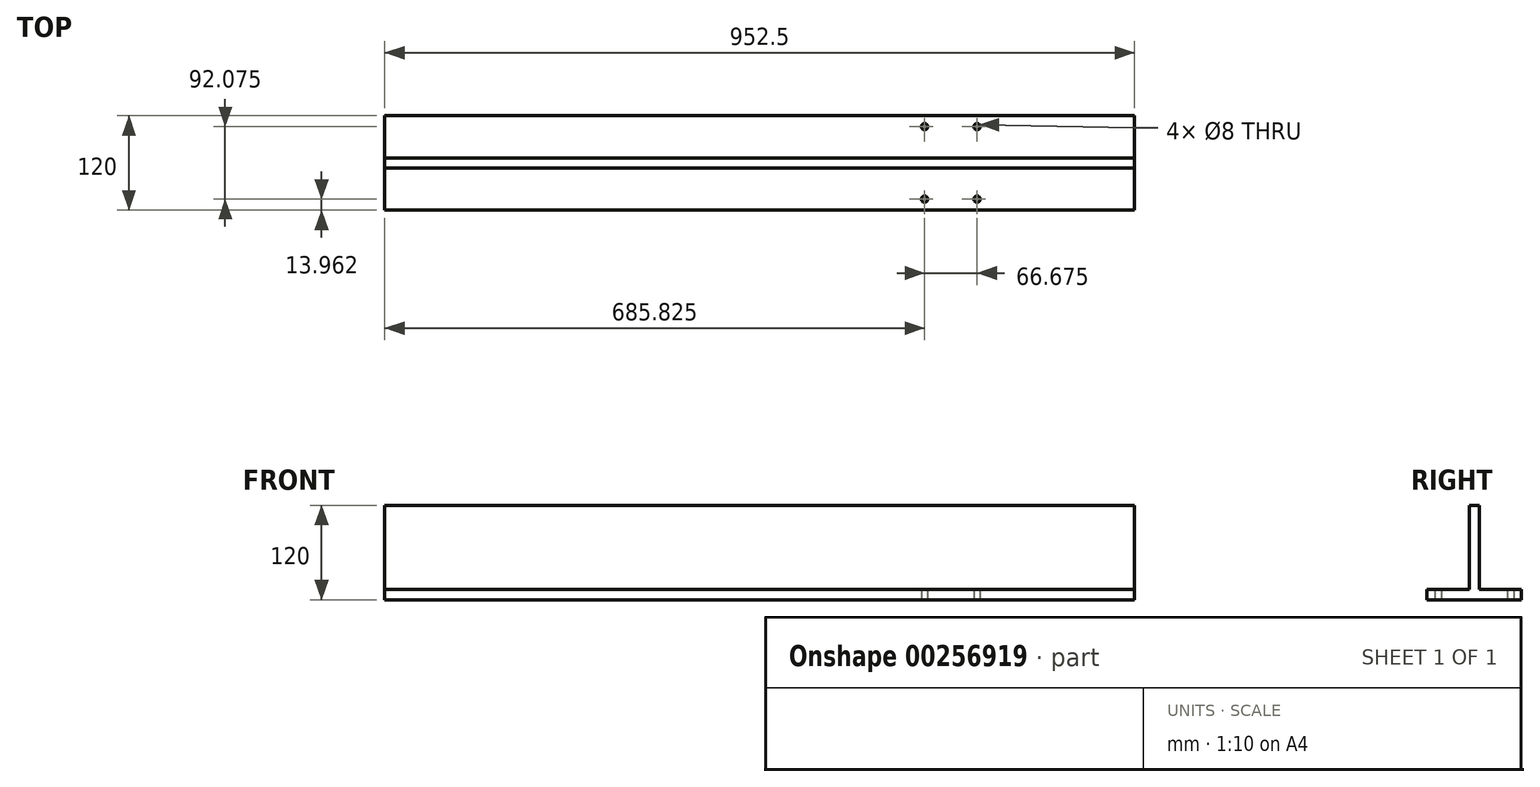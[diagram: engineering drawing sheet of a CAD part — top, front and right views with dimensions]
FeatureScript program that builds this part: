
annotation { "Feature Type Name" : "Feature", "Feature Type Description" : "" }
export const myFeature = defineFeature(function(context is Context, id is Id, definition is map)
    precondition{}
    {
        {
            var Q0;
            Q0=qCreatedBy(makeId("Right.planeOp"),FACE);
            var sketch = newSketch(context, id + "F0", { "sketchPlane" : qUnion([Q0])});
            skLineSegment(sketch, "E0", {"start": v(-60, 0) * mm, "end": v(60, 0) * mm});
            skLineSegment(sketch, "E1", {"start": v(60, 0) * mm, "end": v(60, 13) * mm});
            skLineSegment(sketch, "E2", {"start": v(60, 13) * mm, "end": v(6.5, 13) * mm});
            skLineSegment(sketch, "E3", {"start": v(6.5, 13) * mm, "end": v(6.5, 120) * mm});
            skLineSegment(sketch, "E4", {"start": v(6.5, 120) * mm, "end": v(-6.5, 120) * mm});
            skLineSegment(sketch, "E5", {"start": v(-6.5, 120) * mm, "end": v(-6.5, 13) * mm});
            skLineSegment(sketch, "E6", {"start": v(-6.5, 13) * mm, "end": v(-60, 13) * mm});
            skLineSegment(sketch, "E7", {"start": v(-60, 13) * mm, "end": v(-60, 0) * mm});
            skPoint(sketch, "E8", {"position": v(0, 120) * mm});
            skSolve(sketch);
        }
        {
            var Q0;
            Q0=makeQuery(id+"F0.imprint","IMPRINT",FACE,{"disambiguationData":[TD([[makeQuery(id+"F0.imprint","IMPRINT",EDGE,{"derivedFrom":sQuery(id+"F0.wireOp",EDGE,"E0")}),1.0]])]});
            extrude(context, id + "F1", {"entities" : qUnion([Q0]), "oppositeDirection" : true, "depth" : 952.5 * mm});
        }
        {
            var Q0;
            Q0=qCreatedBy(makeId("Top.planeOp"),FACE);
            var sketch = newSketch(context, id + "F2", { "sketchPlane" : qUnion([Q0])});
            skCircle(sketch, "E9", {"center": v(-200, 46.04) * mm, "radius": 4 * mm});
            skCircle(sketch, "E10", {"center": v(-266.68, 46.04) * mm, "radius": 4 * mm});
            skCircle(sketch, "E11", {"center": v(-266.68, -46.04) * mm, "radius": 4 * mm});
            skCircle(sketch, "E12", {"center": v(-200, -46.04) * mm, "radius": 4 * mm});
            skLineSegment(sketch, "E13", {"start": v(-476.25, 0) * mm, "end": v(-476.25, 155.08) * mm, "construction": true});
            skCircle(sketch, "E14.MirrorC", {"center": v(-685.83, -46.04) * mm, "radius": 4 * mm});
            skCircle(sketch, "E15.MirrorC", {"center": v(-752.5, -46.04) * mm, "radius": 4 * mm});
            skCircle(sketch, "E16.MirrorC", {"center": v(-752.5, 46.04) * mm, "radius": 4 * mm});
            skCircle(sketch, "E17.MirrorC", {"center": v(-685.83, 46.04) * mm, "radius": 4 * mm});
            skSolve(sketch);
        }
        {
            var Q0;
            Q0=makeQuery(id+"F2.imprint","IMPRINT",FACE,{"disambiguationData":[TD([[makeQuery(id+"F2.imprint","IMPRINT",EDGE,{"derivedFrom":sQuery(id+"F2.wireOp",EDGE,"E12")}),1.0]])]});
            var Q1;
            Q1=makeQuery(id+"F2.imprint","IMPRINT",FACE,{"disambiguationData":[TD([[makeQuery(id+"F2.imprint","IMPRINT",EDGE,{"derivedFrom":sQuery(id+"F2.wireOp",EDGE,"E9")}),1.0]])]});
            var Q2;
            Q2=makeQuery(id+"F2.imprint","IMPRINT",FACE,{"disambiguationData":[TD([[makeQuery(id+"F2.imprint","IMPRINT",EDGE,{"derivedFrom":sQuery(id+"F2.wireOp",EDGE,"E10")}),1.0]])]});
            var Q3;
            Q3=makeQuery(id+"F2.imprint","IMPRINT",FACE,{"disambiguationData":[TD([[makeQuery(id+"F2.imprint","IMPRINT",EDGE,{"derivedFrom":sQuery(id+"F2.wireOp",EDGE,"E11")}),1.0]])]});
            var Q4;
            Q4=makeQuery(id+"F2.imprint","IMPRINT",FACE,{"disambiguationData":[TD([[makeQuery(id+"F2.imprint","IMPRINT",EDGE,{"derivedFrom":sQuery(id+"F2.wireOp",EDGE,"E15.MirrorC")}),-1.0]])]});
            var Q5;
            Q5=makeQuery(id+"F2.imprint","IMPRINT",FACE,{"disambiguationData":[TD([[makeQuery(id+"F2.imprint","IMPRINT",EDGE,{"derivedFrom":sQuery(id+"F2.wireOp",EDGE,"E14.MirrorC")}),-1.0]])]});
            var Q6;
            Q6=makeQuery(id+"F2.imprint","IMPRINT",FACE,{"disambiguationData":[TD([[makeQuery(id+"F2.imprint","IMPRINT",EDGE,{"derivedFrom":sQuery(id+"F2.wireOp",EDGE,"E17.MirrorC")}),-1.0]])]});
            var Q7;
            Q7=makeQuery(id+"F2.imprint","IMPRINT",FACE,{"disambiguationData":[TD([[makeQuery(id+"F2.imprint","IMPRINT",EDGE,{"derivedFrom":sQuery(id+"F2.wireOp",EDGE,"E16.MirrorC")}),-1.0]])]});
            var Q8;
            Q8=sQuery(id+"F2.wireOp",EDGE,"E11");
            var Q9;
            Q9=sQuery(id+"F2.wireOp",EDGE,"E12");
            var Q10;
            Q10=sQuery(id+"F2.wireOp",EDGE,"E9");
            var Q11;
            Q11=sQuery(id+"F2.wireOp",EDGE,"E10");
            extrude(context, id + "F3", {"entities" : qUnion([Q0, Q1, Q2, Q3, Q4, Q5, Q6, Q7]), "operationType" : NewBodyOperationType.REMOVE, "surfaceEntities" : qUnion([Q8, Q9, Q10, Q11]), "endBound" : BoundingType.THROUGH_ALL, "depth" : 25.4 * mm});
        }
    });
